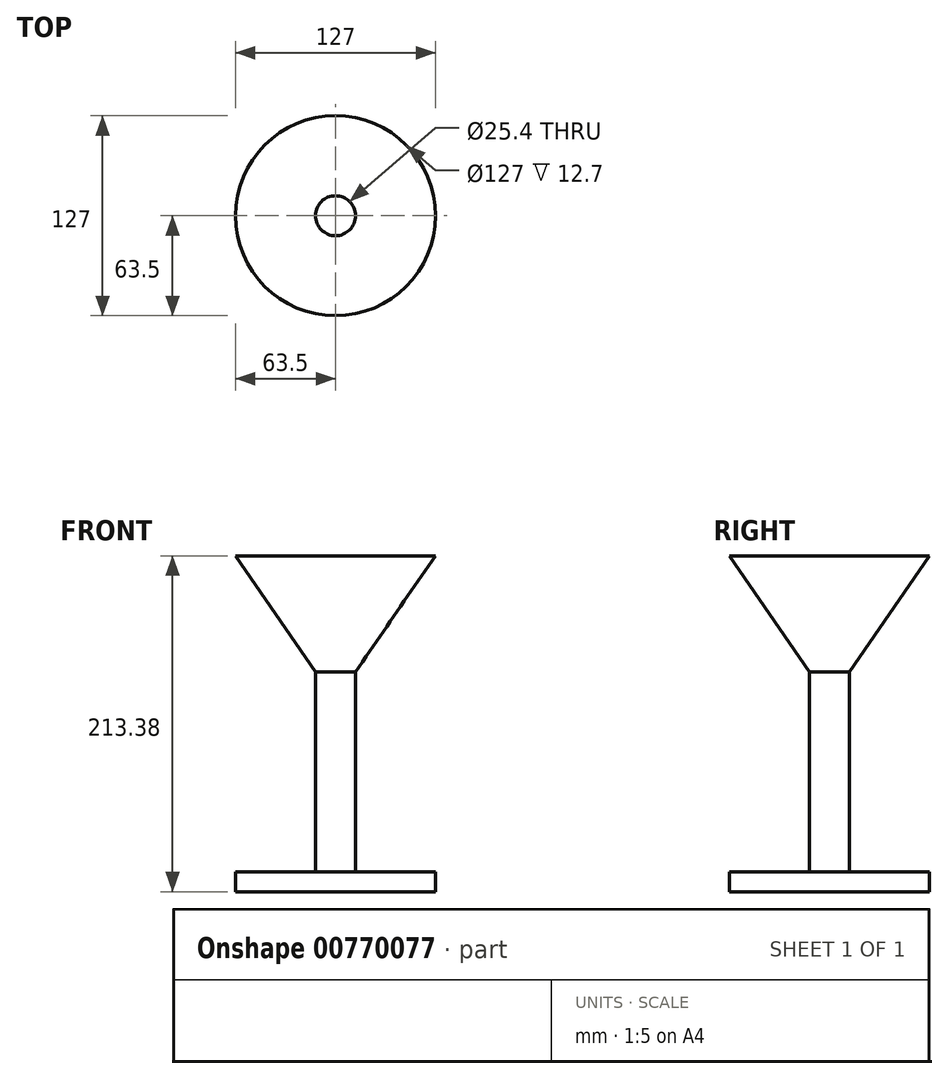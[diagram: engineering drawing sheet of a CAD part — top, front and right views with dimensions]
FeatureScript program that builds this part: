
annotation { "Feature Type Name" : "Feature", "Feature Type Description" : "" }
export const myFeature = defineFeature(function(context is Context, id is Id, definition is map)
    precondition{}
    {
        {
            var Q0;
            Q0=qCreatedBy(makeId("Front.planeOp"),FACE);
            var sketch = newSketch(context, id + "F0", { "sketchPlane" : qUnion([Q0])});
            skLineSegment(sketch, "E0", {"start": v(0, 0) * mm, "end": v(63.5, 0) * mm});
            skLineSegment(sketch, "E1", {"start": v(63.5, 0) * mm, "end": v(63.5, 12.7) * mm});
            skLineSegment(sketch, "E2", {"start": v(63.5, 12.7) * mm, "end": v(12.7, 12.7) * mm});
            skLineSegment(sketch, "E3", {"start": v(12.7, 12.7) * mm, "end": v(12.7, 139.7) * mm});
            skLineSegment(sketch, "E4", {"start": v(12.7, 139.7) * mm, "end": v(63.5, 213.38) * mm});
            skLineSegment(sketch, "E5", {"start": v(63.5, 213.38) * mm, "end": v(0, 213.38) * mm});
            skSolve(sketch);
        }
        {
            var Q0;
            Q0=qCreatedBy(makeId("Front.planeOp"),FACE);
            var sketch = newSketch(context, id + "F1", { "sketchPlane" : qUnion([Q0])});
            skLineSegment(sketch, "E6", {"start": v(0, 0) * mm, "end": v(0, 136.86) * mm});
            skSolve(sketch);
        }
        {
            var Q0;
            Q0=sQuery(id+"F0.wireOp",EDGE,"E4");
            var Q1;
            Q1=sQuery(id+"F0.wireOp",EDGE,"E3");
            var Q2;
            Q2=sQuery(id+"F0.wireOp",EDGE,"E2");
            var Q3;
            Q3=sQuery(id+"F0.wireOp",EDGE,"E1");
            var Q4;
            Q4=sQuery(id+"F0.wireOp",EDGE,"E0");
            var Q5;
            Q5 = qConstructionFilter(qBodyType(qCreatedBy(id + "FDvBvoNpwDSTWwS_1" ,EDGE), BodyType.WIRE), ConstructionObject.NO);
            var Q6;
            Q6=sQuery(id+"F1.wireOp",EDGE,"E6");
            revolve(context, id + "F2", {"bodyType" : ToolBodyType.SURFACE, "surfaceOperationType" : NewSurfaceOperationType.NEW, "surfaceEntities" : qUnion([Q0, Q1, Q2, Q3, Q4, Q5]), "axis" : qUnion([Q6]), "revolveType" : RevolveType.FULL});
        }
    });
